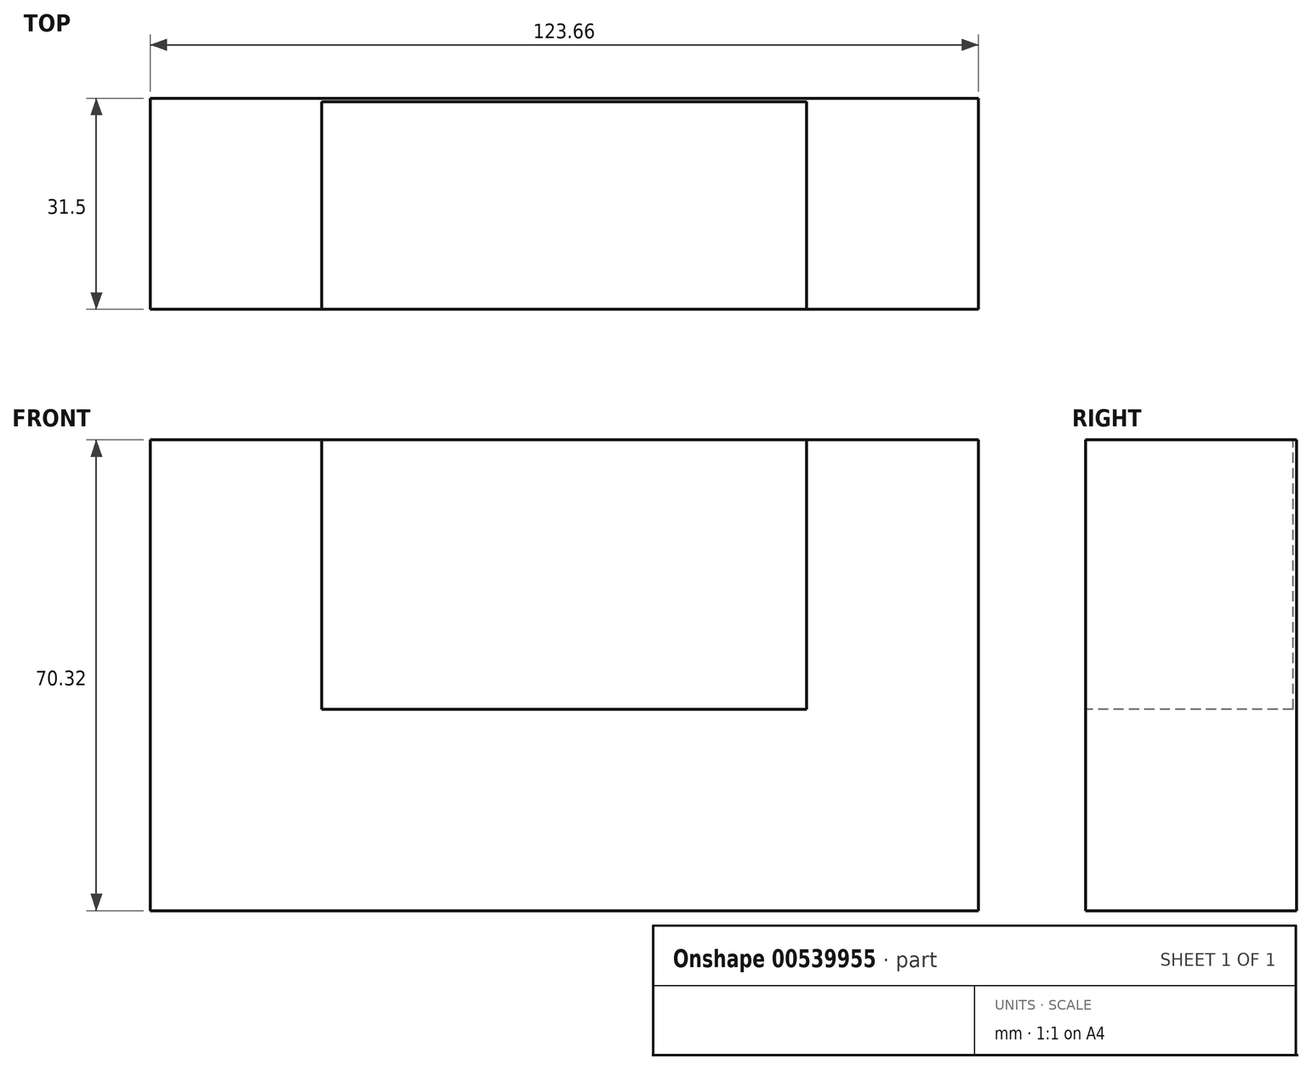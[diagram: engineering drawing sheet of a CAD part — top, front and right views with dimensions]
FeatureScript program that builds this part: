
annotation { "Feature Type Name" : "Feature", "Feature Type Description" : "" }
export const myFeature = defineFeature(function(context is Context, id is Id, definition is map)
    precondition{}
    {
        {
            var Q0;
            Q0=qCreatedBy(makeId("Front.planeOp"),FACE);
            var sketch = newSketch(context, id + "F0", { "sketchPlane" : qUnion([Q0])});
            skLineSegment(sketch, "E0", {"start": v(-59, 14.15) * mm, "end": v(-59, -56.17) * mm});
            skLineSegment(sketch, "E1", {"start": v(-59, -56.17) * mm, "end": v(64.66, -56.17) * mm});
            skLineSegment(sketch, "E2", {"start": v(64.66, -56.17) * mm, "end": v(64.66, 14.15) * mm});
            skLineSegment(sketch, "E3", {"start": v(64.66, 14.15) * mm, "end": v(39.04, 14.15) * mm});
            skLineSegment(sketch, "E4", {"start": v(-59, 14.15) * mm, "end": v(-33.37, 14.15) * mm});
            skLineSegment(sketch, "E5", {"start": v(-33.37, 14.15) * mm, "end": v(-33.37, -26.07) * mm});
            skLineSegment(sketch, "E6", {"start": v(-33.37, -26.07) * mm, "end": v(39.04, -26.07) * mm});
            skLineSegment(sketch, "E7", {"start": v(39.04, -26.07) * mm, "end": v(39.04, 14.15) * mm});
            skSolve(sketch);
        }
        {
            var Q0;
            Q0=makeQuery(id+"F0.imprint","IMPRINT",FACE,{"disambiguationData":[TD([[makeQuery(id+"F0.imprint","IMPRINT",EDGE,{"derivedFrom":sQuery(id+"F0.wireOp",EDGE,"E0")}),1.0]])]});
            extrude(context, id + "F1", {"entities" : qUnion([Q0]), "endBound" : BoundingType.SYMMETRIC, "oppositeDirection" : true, "depth" : 31.5 * mm, "offsetDistance" : 25.4 * mm});
        }
        {
            var Q0;
            Q0=makeQuery(id+"F1.opExtrude","CAP_FACE",FACE,{"disambiguationData":[OSD([sQuery(id+"F0.wireOp",EDGE,"E0"),sQuery(id+"F0.wireOp",EDGE,"E1"),sQuery(id+"F0.wireOp",EDGE,"E2"),sQuery(id+"F0.wireOp",EDGE,"E3"),sQuery(id+"F0.wireOp",EDGE,"E4"),sQuery(id+"F0.wireOp",EDGE,"E5"),sQuery(id+"F0.wireOp",EDGE,"E6"),sQuery(id+"F0.wireOp",EDGE,"E7")])],"isStart":false});
            var sketch = newSketch(context, id + "F2", { "sketchPlane" : qUnion([Q0])});
            skLineSegment(sketch, "E8", {"start": v(-39.04, 14.15) * mm, "end": v(33.37, 14.15) * mm});
            skLineSegment(sketch, "E9", {"start": v(33.37, 14.15) * mm, "end": v(33.37, -26.07) * mm});
            skLineSegment(sketch, "E10", {"start": v(33.37, -26.07) * mm, "end": v(-39.04, -26.07) * mm});
            skLineSegment(sketch, "E11", {"start": v(-39.04, -26.07) * mm, "end": v(-39.04, 14.15) * mm});
            skSolve(sketch);
        }
        {
            var Q0;
            Q0=makeQuery(id+"F2.imprint","IMPRINT",FACE,{"disambiguationData":[TD([[makeQuery(id+"F2.imprint","IMPRINT",EDGE,{"derivedFrom":sQuery(id+"F2.wireOp",EDGE,"E8")}),-1.0]])]});
            extrude(context, id + "F3", {"entities" : qUnion([Q0]), "operationType" : NewBodyOperationType.ADD, "oppositeDirection" : true, "depth" : 0.5 * mm, "offsetDistance" : 25.4 * mm});
        }
    });
